# Revit family: NLRS_63_LD_LUM-DL02IQ-LPBX_luminaid
name_source: partatom
category: Lighting Devices
revit_build: Autodesk Revit 2018 (Build: 20190510_1515(x64)
units: mm (PartAtom-declared; Revit-internal decimal feet)

## family parameters
Always vertical = Yes
Cut with Voids When Loaded = No
Maintain Annotation Orientation = No
Part Type = Normal
Room Calculation Point = No
Round Connector Dimension = Use Diameter
Shared = No
Work Plane-Based = No

## types (1)
- LUM-DL02IQ-LPBX-xxxx
    Ambient temp range = -25°C ~ +35°C
    Angle = 180.00°
    Article code = LUM-DL02IQ-LPBX-xxxx
    Height = 90 mm  [stored 0.295276 ft]
    House = IP65
    Housing material = PS, PA
    Impact Protection Rating = IK07
    Length = 180 mm  [stored 0.590551 ft]
    Manufacturer = LUMINAID B.V.
    Product Brand = DATALUX.LT
    Type = CAP.LOOP
    Upside = No
    Weight = 1.10 kg
    Width = 130 mm  [stored 0.426509 ft]

note: [stored X ft] marks values corroborated as IEEE doubles in the binary element streams (Revit-internal decimal feet)

## geometry (parser evidence)
native form markers: Sweep x8
no freeform markers — native parametric forms only
